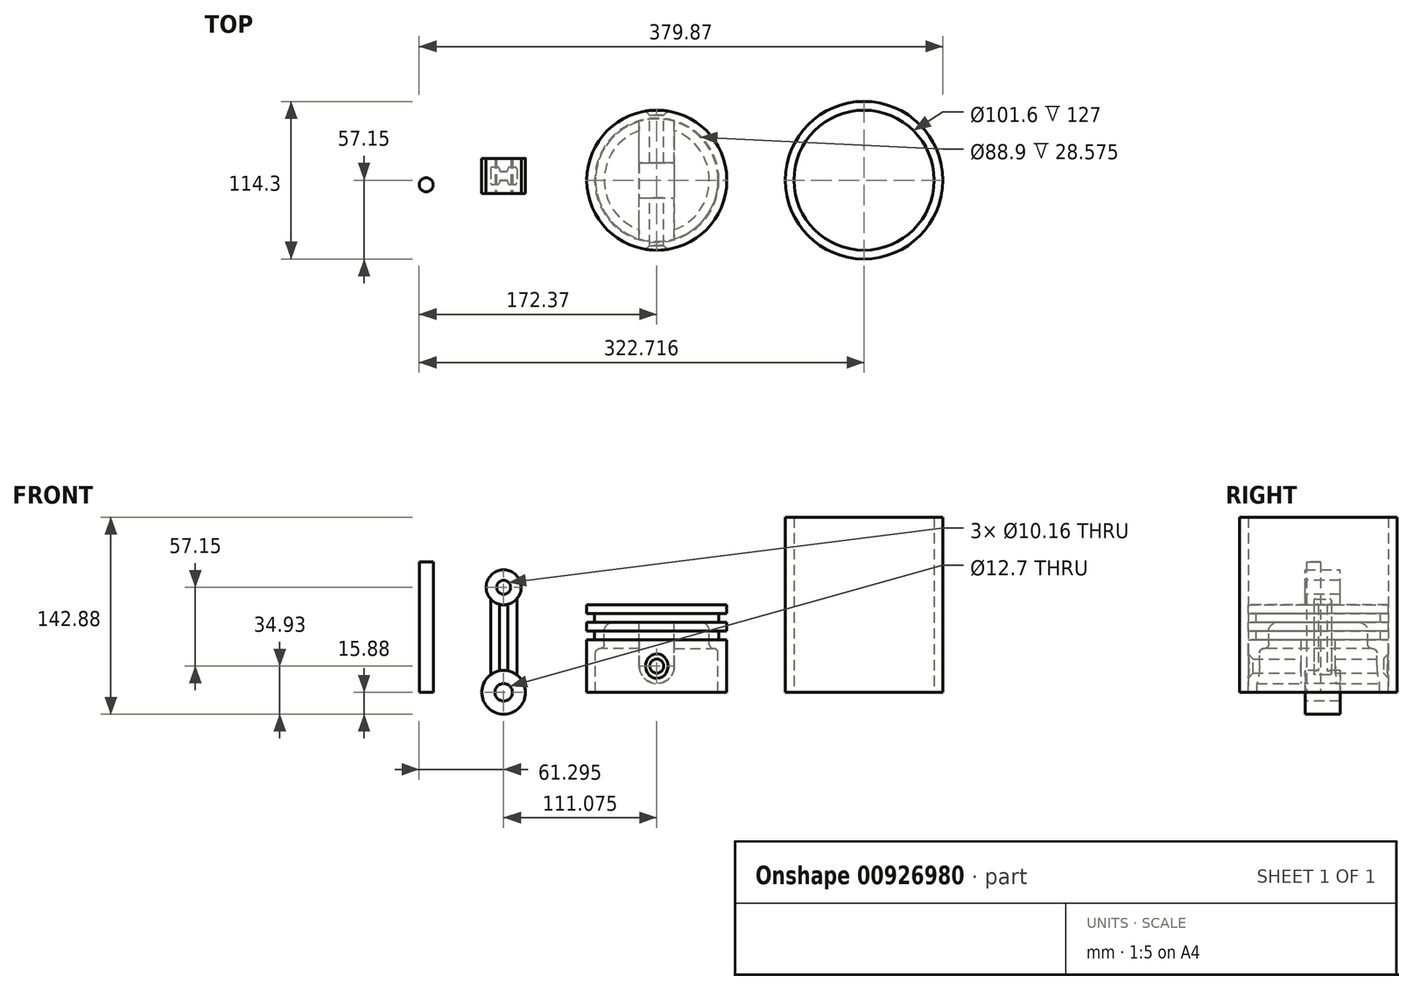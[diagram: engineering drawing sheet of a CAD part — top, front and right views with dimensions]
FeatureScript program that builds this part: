
annotation { "Feature Type Name" : "Feature", "Feature Type Description" : "" }
export const myFeature = defineFeature(function(context is Context, id is Id, definition is map)
    precondition{}
    {
        {
            var Q0;
            Q0=qCreatedBy(makeId("Front.planeOp"),FACE);
            var sketch = newSketch(context, id + "F0", { "sketchPlane" : qUnion([Q0])});
            skLineSegment(sketch, "E0", {"start": v(0, 0) * mm, "end": v(50.8, 0) * mm});
            skLineSegment(sketch, "E1", {"start": v(50.8, 0) * mm, "end": v(50.8, 38.1) * mm});
            skLineSegment(sketch, "E2", {"start": v(50.8, 38.1) * mm, "end": v(45.09, 38.1) * mm});
            skLineSegment(sketch, "E3", {"start": v(45.09, 38.1) * mm, "end": v(45.09, 44.45) * mm});
            skLineSegment(sketch, "E4", {"start": v(45.09, 44.45) * mm, "end": v(50.8, 44.45) * mm});
            skLineSegment(sketch, "E5", {"start": v(50.8, 44.45) * mm, "end": v(50.8, 50.8) * mm});
            skLineSegment(sketch, "E6", {"start": v(50.8, 50.8) * mm, "end": v(45.09, 50.8) * mm});
            skLineSegment(sketch, "E7", {"start": v(45.09, 50.8) * mm, "end": v(45.09, 57.15) * mm});
            skLineSegment(sketch, "E8", {"start": v(45.09, 57.15) * mm, "end": v(50.8, 57.15) * mm});
            skLineSegment(sketch, "E9", {"start": v(50.8, 57.15) * mm, "end": v(50.8, 63.5) * mm});
            skLineSegment(sketch, "E10", {"start": v(50.8, 63.5) * mm, "end": v(0, 63.5) * mm});
            skLineSegment(sketch, "E11", {"start": v(0, 63.5) * mm, "end": v(0, 0) * mm});
            skLineSegment(sketch, "E12", {"start": v(38.1, 34.93) * mm, "end": v(38.1, 44.45) * mm});
            skLineSegment(sketch, "E13", {"start": v(31.75, 50.8) * mm, "end": v(0, 50.8) * mm});
            skPoint(sketch, "E14.visualSharp", {"position": v(38.1, 50.8) * mm});
            skArc(sketch, "E14.filletArc", {"start": v(38.1, 44.45) * mm, "mid": v(36.24, 48.94) * mm, "end": v(31.75, 50.8) * mm});
            skLineSegment(sketch, "E15", {"start": v(44.45, 0) * mm, "end": v(44.45, 28.58) * mm});
            skLineSegment(sketch, "E16", {"start": v(41.28, 31.75) * mm, "end": v(41.27, 31.75) * mm});
            skPoint(sketch, "E17.visualSharp", {"position": v(38.1, 31.75) * mm});
            skArc(sketch, "E17.filletArc", {"start": v(38.1, 34.93) * mm, "mid": v(39.03, 32.68) * mm, "end": v(41.27, 31.75) * mm});
            skPoint(sketch, "E18.visualSharp", {"position": v(44.45, 31.75) * mm});
            skArc(sketch, "E18.filletArc", {"start": v(44.45, 28.58) * mm, "mid": v(43.52, 30.82) * mm, "end": v(41.28, 31.75) * mm});
            skSolve(sketch);
        }
        {
            var Q0;
            {var subQ0=sQuery(id+"F0.wireOp",EDGE,"E1");Q0=makeQuery(id+"F0.imprint","IMPRINT",FACE,{"disambiguationData":[TD([[makeQuery(id+"F0.imprint","IMPRINT",EDGE,{"derivedFrom":subQ0}),1.0]])]});}
            var Q1;
            Q1=sQuery(id+"F0.wireOp",EDGE,"E11");
            revolve(context, id + "F1", {"surfaceOperationType" : NewSurfaceOperationType.NEW, "entities" : qUnion([Q0]), "axis" : qUnion([Q1]), "revolveType" : RevolveType.FULL});
        }
        {
            var Q0;
            Q0=qCreatedBy(makeId("Front.planeOp"),FACE);
            var sketch = newSketch(context, id + "F2", { "sketchPlane" : qUnion([Q0])});
            skLineSegment(sketch, "E19", {"start": v(-12.7, 19.05) * mm, "end": v(-12.7, 63.5) * mm});
            skLineSegment(sketch, "E20", {"start": v(-12.7, 63.5) * mm, "end": v(12.7, 63.5) * mm});
            skLineSegment(sketch, "E21", {"start": v(12.7, 63.5) * mm, "end": v(12.7, 19.05) * mm});
            skPoint(sketch, "E22.end.orphan", {"position": v(12.7, 0) * mm});
            skLineSegment(sketch, "E23", {"start": v(0, 6.35) * mm, "end": v(0, 6.35) * mm});
            skPoint(sketch, "E24.visualSharp", {"position": v(-12.7, 6.35) * mm});
            skArc(sketch, "E24.filletArc", {"start": v(-12.7, 19.05) * mm, "mid": v(-8.98, 10.07) * mm, "end": v(0, 6.35) * mm});
            skPoint(sketch, "E25.visualSharp", {"position": v(12.7, 6.35) * mm});
            skArc(sketch, "E25.filletArc", {"start": v(0, 6.35) * mm, "mid": v(8.98, 10.07) * mm, "end": v(12.7, 19.05) * mm});
            skSolve(sketch);
        }
        {
            var Q0;
            Q0 = qSketchRegion(id + "F2", true);
            extrude(context, id + "F3", {"entities" : qUnion([Q0]), "operationType" : NewBodyOperationType.ADD, "endBound" : BoundingType.SYMMETRIC, "depth" : 101.6 * mm, "offsetDistance" : 25.4 * mm});
        }
        {
            var Q0;
            Q0=makeQuery(id+"F3.opExtrude","CAP_FACE",FACE,{"disambiguationData":[OSD([sQuery(id+"F2.wireOp",EDGE,"E19"),sQuery(id+"F2.wireOp",EDGE,"E20"),sQuery(id+"F2.wireOp",EDGE,"E21"),sQuery(id+"F2.wireOp",EDGE,"E24.filletArc"),sQuery(id+"F2.wireOp",EDGE,"E25.filletArc")])],"isStart":true});
            var sketch = newSketch(context, id + "F4", { "sketchPlane" : qUnion([Q0])});
            skPoint(sketch, "E26", {"position": v(0, 19.05) * mm});
            skSolve(sketch);
        }
        {
            var Q0;
            Q0=sQuery(id+"F4.wireOp",VERTEX,"E26");
            var Q1;
            Q1=makeQuery(id+"F1.opRevolve","SWEPT_BODY",BODY,{"disambiguationData":[OSD([sQuery(id+"F0.wireOp",EDGE,"E0"),sQuery(id+"F0.wireOp",EDGE,"E1"),sQuery(id+"F0.wireOp",EDGE,"E2"),sQuery(id+"F0.wireOp",EDGE,"E3"),sQuery(id+"F0.wireOp",EDGE,"E4"),sQuery(id+"F0.wireOp",EDGE,"E5"),sQuery(id+"F0.wireOp",EDGE,"E6"),sQuery(id+"F0.wireOp",EDGE,"E7"),sQuery(id+"F0.wireOp",EDGE,"E8"),sQuery(id+"F0.wireOp",EDGE,"E9"),sQuery(id+"F0.wireOp",EDGE,"E10"),sQuery(id+"F0.wireOp",EDGE,"E11"),sQuery(id+"F0.wireOp",EDGE,"E12"),sQuery(id+"F0.wireOp",EDGE,"E13"),sQuery(id+"F0.wireOp",EDGE,"E14.filletArc"),sQuery(id+"F0.wireOp",EDGE,"E15"),sQuery(id+"F0.wireOp",EDGE,"E17.filletArc"),sQuery(id+"F0.wireOp",EDGE,"E18.filletArc")])]});
            hole(context, id + "F5", {"style" : HoleStyle.C_SINK, "endStyle" : HoleEndStyle.BLIND, "holeDiameter" : 10.16 * mm, "cSinkDiameter" : 17.78 * mm, "cSinkAngle" : 95 * degree, "majorDiameter" : 6.35 * mm, "holeDepth" : 50.8 * mm, "isTappedThrough" : true, "tappedDepth" : 12.7 * mm, "tapClearance" : 3, "locations" : qUnion([Q0]), "scope" : qUnion([Q1])});
        }
        {
            var Q0;
            Q0=makeQuery(id+"F3.opExtrude","CAP_FACE",FACE,{"disambiguationData":[OSD([sQuery(id+"F2.wireOp",EDGE,"E19"),sQuery(id+"F2.wireOp",EDGE,"E20"),sQuery(id+"F2.wireOp",EDGE,"E21"),sQuery(id+"F2.wireOp",EDGE,"E24.filletArc"),sQuery(id+"F2.wireOp",EDGE,"E25.filletArc")])],"isStart":false});
            var sketch = newSketch(context, id + "F6", { "sketchPlane" : qUnion([Q0])});
            skPoint(sketch, "E27", {"position": v(0, 19.05) * mm});
            skSolve(sketch);
        }
        {
            var Q0;
            Q0=sQuery(id+"F6.wireOp",VERTEX,"E27");
            var Q1;
            Q1=makeQuery(id+"F1.opRevolve","SWEPT_BODY",BODY,{"disambiguationData":[OSD([sQuery(id+"F0.wireOp",EDGE,"E0"),sQuery(id+"F0.wireOp",EDGE,"E1"),sQuery(id+"F0.wireOp",EDGE,"E2"),sQuery(id+"F0.wireOp",EDGE,"E3"),sQuery(id+"F0.wireOp",EDGE,"E4"),sQuery(id+"F0.wireOp",EDGE,"E5"),sQuery(id+"F0.wireOp",EDGE,"E6"),sQuery(id+"F0.wireOp",EDGE,"E7"),sQuery(id+"F0.wireOp",EDGE,"E8"),sQuery(id+"F0.wireOp",EDGE,"E9"),sQuery(id+"F0.wireOp",EDGE,"E10"),sQuery(id+"F0.wireOp",EDGE,"E11"),sQuery(id+"F0.wireOp",EDGE,"E12"),sQuery(id+"F0.wireOp",EDGE,"E13"),sQuery(id+"F0.wireOp",EDGE,"E14.filletArc"),sQuery(id+"F0.wireOp",EDGE,"E15"),sQuery(id+"F0.wireOp",EDGE,"E17.filletArc"),sQuery(id+"F0.wireOp",EDGE,"E18.filletArc")])]});
            hole(context, id + "F7", {"style" : HoleStyle.C_SINK, "endStyle" : HoleEndStyle.BLIND, "holeDiameter" : 10.16 * mm, "cSinkDiameter" : 17.78 * mm, "cSinkAngle" : 95 * degree, "majorDiameter" : 6.35 * mm, "holeDepth" : 50.8 * mm, "isTappedThrough" : true, "tappedDepth" : 12.7 * mm, "tapClearance" : 3, "locations" : qUnion([Q0]), "scope" : qUnion([Q1])});
        }
        {
            var Q0;
            Q0=qCreatedBy(makeId("Right.planeOp"),FACE);
            var sketch = newSketch(context, id + "F8", { "sketchPlane" : qUnion([Q0])});
            skLineSegment(sketch, "E28", {"start": v(50.8, 0) * mm, "end": v(50.8, 38.1) * mm});
            skLineSegment(sketch, "E29", {"start": v(50.8, 38.1) * mm, "end": v(45.09, 38.1) * mm});
            skLineSegment(sketch, "E30", {"start": v(45.09, 38.1) * mm, "end": v(45.09, 44.45) * mm});
            skLineSegment(sketch, "E31", {"start": v(45.09, 44.45) * mm, "end": v(50.8, 44.45) * mm});
            skLineSegment(sketch, "E32", {"start": v(50.8, 44.45) * mm, "end": v(50.8, 50.8) * mm});
            skLineSegment(sketch, "E33", {"start": v(50.8, 50.8) * mm, "end": v(45.09, 50.8) * mm});
            skLineSegment(sketch, "E34", {"start": v(45.09, 50.8) * mm, "end": v(45.09, 57.15) * mm});
            skLineSegment(sketch, "E35", {"start": v(45.09, 57.15) * mm, "end": v(50.8, 57.15) * mm});
            skLineSegment(sketch, "E36", {"start": v(50.8, 57.15) * mm, "end": v(50.8, 63.5) * mm});
            skPoint(sketch, "E37.visualSharp", {"position": v(64.44, 47.34) * mm});
            skLineSegment(sketch, "E38", {"start": v(67.62, 31.75) * mm, "end": v(67.62, 31.75) * mm});
            skPoint(sketch, "E39.visualSharp", {"position": v(64.44, 31.75) * mm});
            skPoint(sketch, "E40.visualSharp", {"position": v(70.8, 31.75) * mm});
            skPoint(sketch, "E37.filletArc.start.orphan", {"position": v(64.44, 44.45) * mm});
            skLineSegment(sketch, "E41", {"start": v(50.8, 0) * mm, "end": v(57.15, 0) * mm});
            skLineSegment(sketch, "E42", {"start": v(57.15, 0) * mm, "end": v(57.15, 63.5) * mm});
            skLineSegment(sketch, "E43", {"start": v(57.15, 63.5) * mm, "end": v(50.8, 63.5) * mm});
            skLineSegment(sketch, "E44", {"start": v(0, 63.5) * mm, "end": v(0, 0) * mm});
            skSolve(sketch);
        }
        {
            var Q0;
            Q0 = qSketchRegion(id + "F8", true);
            var Q1;
            Q1=sQuery(id+"F8.wireOp",EDGE,"E44");
            revolve(context, id + "F9", {"operationType" : NewBodyOperationType.REMOVE, "surfaceOperationType" : NewSurfaceOperationType.NEW, "entities" : qUnion([Q0]), "axis" : qUnion([Q1]), "revolveType" : RevolveType.FULL, "oppositeDirection" : true});
        }
        {
            var Q0;
            Q0=qCreatedBy(makeId("Right.planeOp"),FACE);
            var sketch = newSketch(context, id + "F10", { "sketchPlane" : qUnion([Q0])});
            skLineSegment(sketch, "E45", {"start": v(12.7, 0.05) * mm, "end": v(-12.7, -0.05) * mm});
            skLineSegment(sketch, "E46", {"start": v(12.7, 0.05) * mm, "end": v(12.54, 38.15) * mm});
            skLineSegment(sketch, "E47", {"start": v(12.54, 38.15) * mm, "end": v(-12.7, 38.05) * mm});
            skLineSegment(sketch, "E48", {"start": v(-12.7, 38.05) * mm, "end": v(-12.7, -0.05) * mm});
            skSolve(sketch);
        }
        {
            var Q0;
            Q0 = qSketchRegion(id + "F10", true);
            extrude(context, id + "F11", {"entities" : qUnion([Q0]), "operationType" : NewBodyOperationType.REMOVE, "endBound" : BoundingType.SYMMETRIC, "oppositeDirection" : true, "depth" : 25.4 * mm, "offsetDistance" : 25.4 * mm});
        }
        {
            var Q0;
            Q0=qCreatedBy(makeId("Top.planeOp"),FACE);
            var sketch = newSketch(context, id + "F12", { "sketchPlane" : qUnion([Q0])});
            skLineSegment(sketch, "E49", {"start": v(-101.55, 3.17) * mm, "end": v(-101.55, -1.9) * mm});
            skLineSegment(sketch, "E50", {"start": v(-102.82, -3.18) * mm, "end": v(-106.63, -3.18) * mm});
            skLineSegment(sketch, "E51", {"start": v(-107.9, -1.9) * mm, "end": v(-107.9, -1.27) * mm});
            skLineSegment(sketch, "E52", {"start": v(-109.17, 0) * mm, "end": v(-112.98, 0) * mm});
            skLineSegment(sketch, "E53", {"start": v(-114.25, -1.27) * mm, "end": v(-114.25, -1.9) * mm});
            skLineSegment(sketch, "E54", {"start": v(-115.52, -3.18) * mm, "end": v(-119.33, -3.18) * mm});
            skLineSegment(sketch, "E55", {"start": v(-120.6, -1.9) * mm, "end": v(-120.6, 3.17) * mm});
            skLineSegment(sketch, "E56", {"start": v(-120.6, 3.17) * mm, "end": v(-101.55, 3.17) * mm});
            skPoint(sketch, "E57.visualSharp", {"position": v(-114.25, 0) * mm});
            skArc(sketch, "E57.filletArc", {"start": v(-112.98, 0) * mm, "mid": v(-113.88, -0.37) * mm, "end": v(-114.25, -1.27) * mm});
            skPoint(sketch, "E58.visualSharp", {"position": v(-107.9, 0) * mm});
            skArc(sketch, "E58.filletArc", {"start": v(-107.9, -1.27) * mm, "mid": v(-108.27, -0.37) * mm, "end": v(-109.17, 0) * mm});
            skPoint(sketch, "E59.visualSharp", {"position": v(-107.9, -3.18) * mm});
            skArc(sketch, "E59.filletArc", {"start": v(-107.9, -1.9) * mm, "mid": v(-107.53, -2.8) * mm, "end": v(-106.63, -3.18) * mm});
            skPoint(sketch, "E60.visualSharp", {"position": v(-114.25, -3.18) * mm});
            skArc(sketch, "E60.filletArc", {"start": v(-115.52, -3.18) * mm, "mid": v(-114.62, -2.8) * mm, "end": v(-114.25, -1.9) * mm});
            skPoint(sketch, "E61.visualSharp", {"position": v(-120.6, -3.18) * mm});
            skArc(sketch, "E61.filletArc", {"start": v(-120.6, -1.9) * mm, "mid": v(-120.23, -2.8) * mm, "end": v(-119.33, -3.18) * mm});
            skPoint(sketch, "E62.visualSharp", {"position": v(-101.55, -3.18) * mm});
            skArc(sketch, "E62.filletArc", {"start": v(-102.82, -3.18) * mm, "mid": v(-101.92, -2.8) * mm, "end": v(-101.55, -1.9) * mm});
            skLineSegment(sketch, "E63.MirrorCS", {"start": v(-101.55, 3.17) * mm, "end": v(-101.55, 8.25) * mm});
            skArc(sketch, "E64.MirrorCS", {"start": v(-102.82, 9.52) * mm, "mid": v(-101.92, 9.15) * mm, "end": v(-101.55, 8.25) * mm});
            skLineSegment(sketch, "E65.MirrorCS", {"start": v(-102.82, 9.52) * mm, "end": v(-106.63, 9.52) * mm});
            skLineSegment(sketch, "E66.MirrorCS", {"start": v(-107.9, 8.25) * mm, "end": v(-107.9, 7.62) * mm});
            skArc(sketch, "E67.MirrorCS", {"start": v(-107.9, 7.62) * mm, "mid": v(-108.27, 6.72) * mm, "end": v(-109.17, 6.35) * mm});
            skLineSegment(sketch, "E68.MirrorCS", {"start": v(-109.17, 6.35) * mm, "end": v(-112.98, 6.35) * mm});
            skArc(sketch, "E69.MirrorCS", {"start": v(-112.98, 6.35) * mm, "mid": v(-113.88, 6.72) * mm, "end": v(-114.25, 7.62) * mm});
            skLineSegment(sketch, "E70.MirrorCS", {"start": v(-114.25, 7.62) * mm, "end": v(-114.25, 8.25) * mm});
            skArc(sketch, "E71.MirrorCS", {"start": v(-115.52, 9.52) * mm, "mid": v(-114.62, 9.15) * mm, "end": v(-114.25, 8.25) * mm});
            skLineSegment(sketch, "E72.MirrorCS", {"start": v(-115.52, 9.52) * mm, "end": v(-119.33, 9.52) * mm});
            skArc(sketch, "E73.MirrorCS", {"start": v(-120.6, 8.25) * mm, "mid": v(-120.23, 9.15) * mm, "end": v(-119.33, 9.52) * mm});
            skLineSegment(sketch, "E74.MirrorCS", {"start": v(-120.6, 8.25) * mm, "end": v(-120.6, 3.17) * mm});
            skPoint(sketch, "E75.MirrorP", {"position": v(-107.9, 9.52) * mm});
            skArc(sketch, "E76.MirrorCS", {"start": v(-107.9, 8.25) * mm, "mid": v(-107.53, 9.15) * mm, "end": v(-106.63, 9.52) * mm});
            skSolve(sketch);
        }
        {
            var Q0;
            Q0=makeQuery(id+"F12.imprint","IMPRINT",FACE,{"disambiguationData":[TD([[makeQuery(id+"F12.imprint","IMPRINT",EDGE,{"derivedFrom":sQuery(id+"F12.wireOp",EDGE,"E56")}),1.0]])]});
            var Q1;
            Q1=makeQuery(id+"F12.imprint","IMPRINT",FACE,{"disambiguationData":[TD([[makeQuery(id+"F12.imprint","IMPRINT",EDGE,{"derivedFrom":sQuery(id+"F12.wireOp",EDGE,"E49")}),-1.0]])]});
            extrude(context, id + "F13", {"entities" : qUnion([Q0, Q1]), "depth" : 76.2 * mm, "offsetDistance" : 25.4 * mm});
        }
        {
            var Q0;
            Q0=makeQuery(id+"F13.opExtrude","SWEPT_FACE",FACE,{"disambiguationData":[OSD([sQuery(id+"F12.wireOp",EDGE,"E54")])]});
            cPlane(context, id + "F14", {"entities" : qUnion([Q0]), "cplaneType" : CPlaneType.OFFSET, "offset" : 6.35 * mm, "oppositeDirection" : true, "width" : 152.4 * mm, "height" : 152.4 * mm});
        }
        {
            var Q0;
            Q0=qCreatedBy(id+"F14.planeOp",FACE);
            var sketch = newSketch(context, id + "F15", { "sketchPlane" : qUnion([Q0])});
            skCircle(sketch, "E77", {"center": v(-111.08, 76.2) * mm, "radius": 12.7 * mm});
            skSolve(sketch);
        }
        {
            var Q0;
            Q0 = qSketchRegion(id + "F15", true);
            extrude(context, id + "F16", {"entities" : qUnion([Q0]), "operationType" : NewBodyOperationType.ADD, "endBound" : BoundingType.SYMMETRIC, "depth" : 25.4 * mm, "offsetDistance" : 25.4 * mm});
        }
        {
            var Q0;
            Q0=makeQuery(id+"F16.opExtrude","CAP_FACE",FACE,{"disambiguationData":[OSD([sQuery(id+"F15.wireOp",EDGE,"E77")])],"isStart":false});
            var sketch = newSketch(context, id + "F17", { "sketchPlane" : qUnion([Q0])});
            skCircle(sketch, "E78", {"center": v(-111.08, 76.2) * mm, "radius": 5.08 * mm});
            skSolve(sketch);
        }
        {
            var Q0;
            Q0 = qSketchRegion(id + "F17", true);
            extrude(context, id + "F18", {"entities" : qUnion([Q0]), "operationType" : NewBodyOperationType.REMOVE, "oppositeDirection" : true, "depth" : 25.4 * mm, "offsetDistance" : 25.4 * mm});
        }
        {
            var Q0;
            Q0=qCreatedBy(id+"F14.planeOp",FACE);
            var sketch = newSketch(context, id + "F19", { "sketchPlane" : qUnion([Q0])});
            skCircle(sketch, "E79", {"center": v(-111.08, 0) * mm, "radius": 15.88 * mm});
            skCircle(sketch, "E80", {"center": v(-111.08, 0) * mm, "radius": 6.35 * mm});
            skSolve(sketch);
        }
        {
            var Q0;
            Q0=makeQuery(id+"F19.imprint","IMPRINT",FACE,{"disambiguationData":[TD([[makeQuery(id+"F19.imprint","IMPRINT",EDGE,{"derivedFrom":sQuery(id+"F19.wireOp",EDGE,"E79")}),1.0]])]});
            extrude(context, id + "F20", {"entities" : qUnion([Q0]), "operationType" : NewBodyOperationType.ADD, "endBound" : BoundingType.SYMMETRIC, "oppositeDirection" : true, "depth" : 25.4 * mm, "offsetDistance" : 25.4 * mm});
        }
        {
            var Q0;
            Q0=makeQuery(id+"F20.opExtrude","CAP_FACE",FACE,{"disambiguationData":[OSD([sQuery(id+"F19.wireOp",EDGE,"E79"),sQuery(id+"F19.wireOp",EDGE,"E80")])],"isStart":true});
            var sketch = newSketch(context, id + "F21", { "sketchPlane" : qUnion([Q0])});
            skCircle(sketch, "E81", {"center": v(-111.08, 0) * mm, "radius": 6.35 * mm});
            skSolve(sketch);
        }
        {
            var Q0;
            Q0 = qSketchRegion(id + "F21", true);
            extrude(context, id + "F22", {"entities" : qUnion([Q0]), "operationType" : NewBodyOperationType.REMOVE, "oppositeDirection" : true, "depth" : 25.4 * mm, "offsetDistance" : 25.4 * mm});
        }
        {
            var Q0;
            Q0=qCreatedBy(makeId("Top.planeOp"),FACE);
            var sketch = newSketch(context, id + "F23", { "sketchPlane" : qUnion([Q0])});
            skCircle(sketch, "E82", {"center": v(-167.29, -3.32) * mm, "radius": 5.08 * mm});
            skSolve(sketch);
        }
        {
            var Q0;
            Q0 = qSketchRegion(id + "F23", true);
            extrude(context, id + "F24", {"entities" : qUnion([Q0]), "depth" : 94.62 * mm, "offsetDistance" : 25.4 * mm});
        }
        {
            var Q0;
            Q0=qCreatedBy(makeId("Top.planeOp"),FACE);
            var sketch = newSketch(context, id + "F25", { "sketchPlane" : qUnion([Q0])});
            skCircle(sketch, "E83", {"center": v(150.35, 0) * mm, "radius": 50.8 * mm});
            skCircle(sketch, "E84.0", {"center": v(150.35, 0) * mm, "radius": 57.15 * mm});
            skSolve(sketch);
        }
        {
            var Q0;
            Q0=makeQuery(id+"F25.imprint","IMPRINT",FACE,{"disambiguationData":[TD([[makeQuery(id+"F25.imprint","IMPRINT",EDGE,{"derivedFrom":sQuery(id+"F25.wireOp",EDGE,"E83")}),-1.0]])]});
            extrude(context, id + "F26", {"entities" : qUnion([Q0]), "depth" : 127 * mm, "offsetDistance" : 25.4 * mm});
        }
    });
